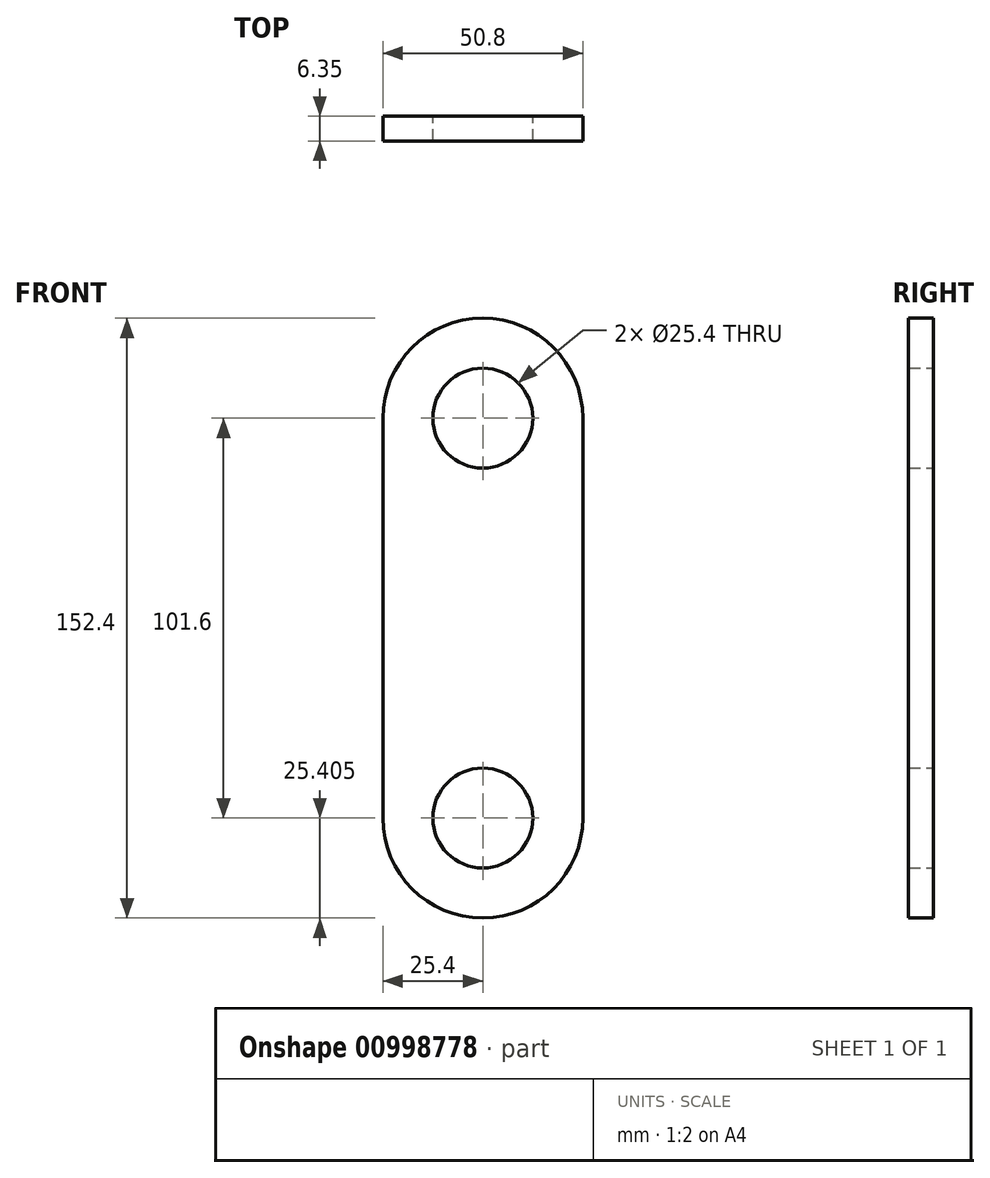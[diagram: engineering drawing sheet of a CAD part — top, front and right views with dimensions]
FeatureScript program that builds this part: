
annotation { "Feature Type Name" : "Feature", "Feature Type Description" : "" }
export const myFeature = defineFeature(function(context is Context, id is Id, definition is map)
    precondition{}
    {
        {
            var Q0;
            Q0=qCreatedBy(makeId("Front.planeOp"),FACE);
            var sketch = newSketch(context, id + "F0", { "sketchPlane" : qUnion([Q0])});
            skCircle(sketch, "E0", {"center": v(0, -34.94) * mm, "radius": 12.7 * mm});
            skLineSegment(sketch, "E1", {"start": v(0, -34.94) * mm, "end": v(0, 66.66) * mm});
            skCircle(sketch, "E2", {"center": v(0, 66.66) * mm, "radius": 12.7 * mm});
            skCircle(sketch, "E3", {"center": v(0, -34.94) * mm, "radius": 25.4 * mm});
            skCircle(sketch, "E4", {"center": v(0, 66.66) * mm, "radius": 25.4 * mm});
            skLineSegment(sketch, "E5", {"start": v(0, 66.66) * mm, "end": v(-25.4, 66.66) * mm});
            skLineSegment(sketch, "E6", {"start": v(-25.4, 66.66) * mm, "end": v(-25.4, -34.94) * mm});
            skLineSegment(sketch, "E7", {"start": v(-25.4, -34.94) * mm, "end": v(0, -34.94) * mm});
            skLineSegment(sketch, "E8", {"start": v(25.4, -34.94) * mm, "end": v(25.4, 66.66) * mm});
            skLineSegment(sketch, "E9", {"start": v(25.4, 66.66) * mm, "end": v(0, 66.66) * mm});
            skLineSegment(sketch, "E10", {"start": v(0, -34.94) * mm, "end": v(25.4, -34.94) * mm});
            skSolve(sketch);
        }
        {
            var Q0;
            {var subQ0=sQuery(id+"F0.wireOp",EDGE,"E5");var subQ1=sQuery(id+"F0.wireOp",EDGE,"E2");var subQ2=makeQuery(id+"F0.imprint","INTERSECT",VERTEX,{"derivedFrom":[subQ1,subQ0]});Q0=makeQuery(id+"F0.imprint","IMPRINT",FACE,{"disambiguationData":[TD([[makeQuery(id+"F0.imprint","IMPRINT",EDGE,{"disambiguationData":[TD([[subQ2,1.0]])],"derivedFrom":subQ1}),-1.0]])]});}
            var Q1;
            {var subQ0=sQuery(id+"F0.wireOp",EDGE,"E4");var subQ1=sQuery(id+"F0.wireOp",EDGE,"E1");var subQ2=makeQuery(id+"F0.imprint","INTERSECT",VERTEX,{"derivedFrom":[subQ1,subQ0]});Q1=makeQuery(id+"F0.imprint","IMPRINT",FACE,{"disambiguationData":[TD([[makeQuery(id+"F0.imprint","IMPRINT",EDGE,{"disambiguationData":[TD([[subQ2,-1.0]])],"derivedFrom":subQ1}),1.0]])]});}
            var Q2;
            {var subQ0=sQuery(id+"F0.wireOp",EDGE,"E4");var subQ1=sQuery(id+"F0.wireOp",EDGE,"E1");var subQ2=makeQuery(id+"F0.imprint","INTERSECT",VERTEX,{"derivedFrom":[subQ1,subQ0]});Q2=makeQuery(id+"F0.imprint","IMPRINT",FACE,{"disambiguationData":[TD([[makeQuery(id+"F0.imprint","IMPRINT",EDGE,{"disambiguationData":[TD([[subQ2,-1.0]])],"derivedFrom":subQ1}),-1.0]])]});}
            var Q3;
            {var subQ5=sQuery(id+"F0.wireOp",EDGE,"E8");Q3=makeQuery(id+"F0.imprint","IMPRINT",FACE,{"disambiguationData":[TD([[makeQuery(id+"F0.imprint","IMPRINT",EDGE,{"derivedFrom":subQ5}),1.0]])]});}
            var Q4;
            {var subQ5=sQuery(id+"F0.wireOp",EDGE,"E6");Q4=makeQuery(id+"F0.imprint","IMPRINT",FACE,{"disambiguationData":[TD([[makeQuery(id+"F0.imprint","IMPRINT",EDGE,{"derivedFrom":subQ5}),1.0]])]});}
            var Q5;
            {var subQ0=sQuery(id+"F0.wireOp",EDGE,"E1");var subQ1=sQuery(id+"F0.wireOp",EDGE,"E0");var subQ2=makeQuery(id+"F0.imprint","INTERSECT",VERTEX,{"derivedFrom":[subQ1,subQ0]});Q5=makeQuery(id+"F0.imprint","IMPRINT",FACE,{"disambiguationData":[TD([[makeQuery(id+"F0.imprint","IMPRINT",EDGE,{"disambiguationData":[TD([[subQ2,-1.0]])],"derivedFrom":subQ1}),-1.0]])]});}
            var Q6;
            {var subQ0=sQuery(id+"F0.wireOp",EDGE,"E1");var subQ1=sQuery(id+"F0.wireOp",EDGE,"E0");var subQ2=makeQuery(id+"F0.imprint","INTERSECT",VERTEX,{"derivedFrom":[subQ1,subQ0]});Q6=makeQuery(id+"F0.imprint","IMPRINT",FACE,{"disambiguationData":[TD([[makeQuery(id+"F0.imprint","IMPRINT",EDGE,{"disambiguationData":[TD([[subQ2,1.0]])],"derivedFrom":subQ1}),-1.0]])]});}
            var Q7;
            {var subQ0=sQuery(id+"F0.wireOp",EDGE,"E10");var subQ1=sQuery(id+"F0.wireOp",EDGE,"E0");var subQ2=makeQuery(id+"F0.imprint","INTERSECT",VERTEX,{"derivedFrom":[subQ1,subQ0]});Q7=makeQuery(id+"F0.imprint","IMPRINT",FACE,{"disambiguationData":[TD([[makeQuery(id+"F0.imprint","IMPRINT",EDGE,{"disambiguationData":[TD([[subQ2,1.0]])],"derivedFrom":subQ1}),-1.0]])]});}
            extrude(context, id + "F1", {"entities" : qUnion([Q0, Q1, Q2, Q3, Q4, Q5, Q6, Q7]), "depth" : 6.35 * mm, "offsetDistance" : 25.4 * mm});
        }
    });
